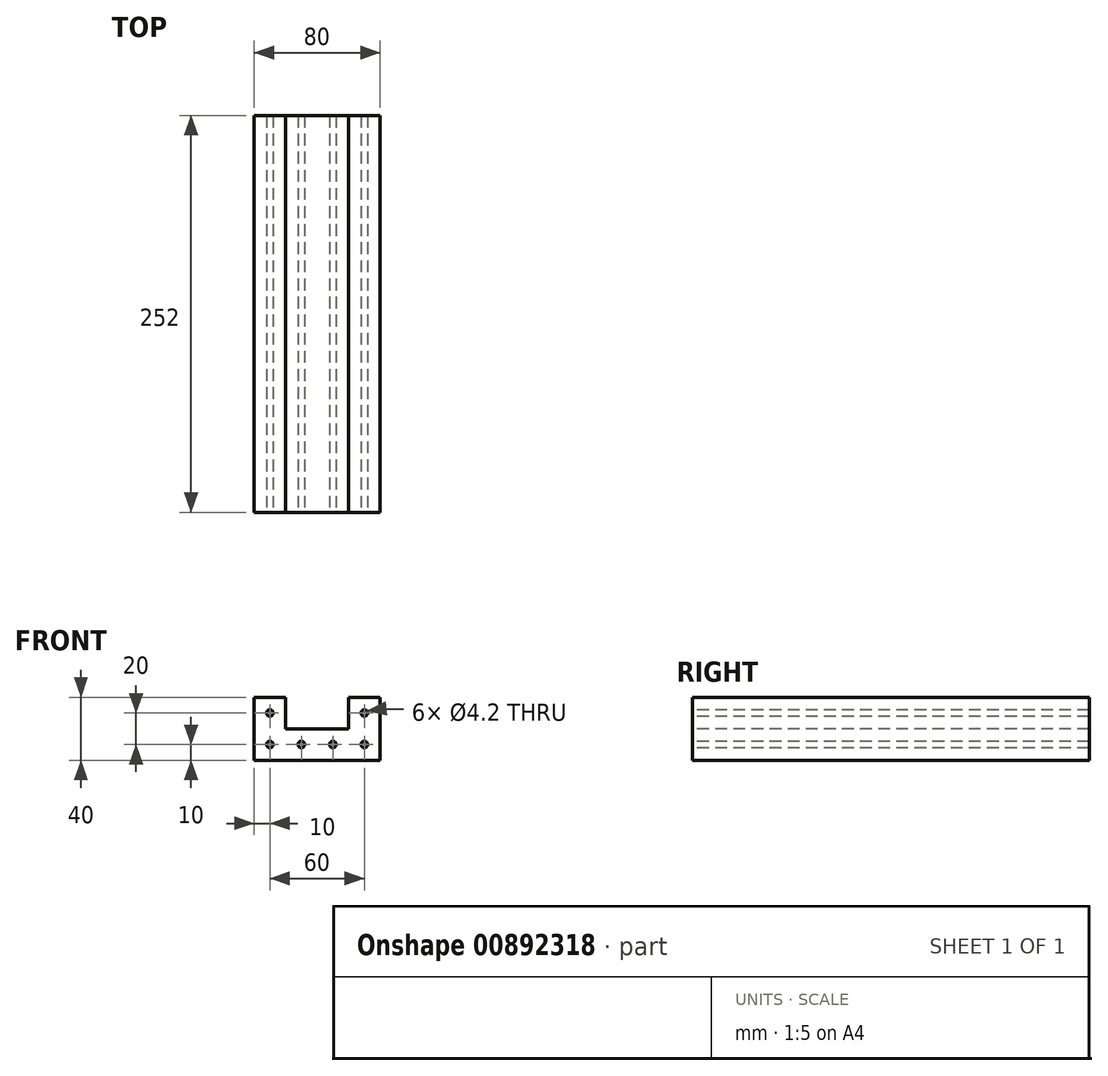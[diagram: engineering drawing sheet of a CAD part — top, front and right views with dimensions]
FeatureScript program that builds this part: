
annotation { "Feature Type Name" : "Feature", "Feature Type Description" : "" }
export const myFeature = defineFeature(function(context is Context, id is Id, definition is map)
    precondition{}
    {
        {
            var Q0;
            Q0=qCreatedBy(makeId("Front.planeOp"),FACE);
            var sketch = newSketch(context, id + "F0", { "sketchPlane" : qUnion([Q0])});
            skLineSegment(sketch, "E0", {"start": v(-40, 40) * mm, "end": v(-40, 0) * mm});
            skLineSegment(sketch, "E1", {"start": v(-40, 0) * mm, "end": v(40, 0) * mm});
            skLineSegment(sketch, "E2", {"start": v(40, 0) * mm, "end": v(40, 40) * mm});
            skLineSegment(sketch, "E3", {"start": v(40, 40) * mm, "end": v(20, 40) * mm});
            skLineSegment(sketch, "E4", {"start": v(20, 40) * mm, "end": v(20, 20) * mm});
            skLineSegment(sketch, "E5", {"start": v(20, 20) * mm, "end": v(-20, 20) * mm});
            skLineSegment(sketch, "E6", {"start": v(-20, 20) * mm, "end": v(-20, 40) * mm});
            skLineSegment(sketch, "E7", {"start": v(-20, 40) * mm, "end": v(-40, 40) * mm});
            skLineSegment(sketch, "E8", {"start": v(-30, 40) * mm, "end": v(-30, 10) * mm, "construction": true});
            skLineSegment(sketch, "E9", {"start": v(-30, 10) * mm, "end": v(30, 10) * mm, "construction": true});
            skLineSegment(sketch, "E10", {"start": v(30, 10) * mm, "end": v(30, 40) * mm, "construction": true});
            skCircle(sketch, "E11", {"center": v(-30, 30) * mm, "radius": 2.1 * mm});
            skCircle(sketch, "E12", {"center": v(-30, 10) * mm, "radius": 2.1 * mm});
            skCircle(sketch, "E13", {"center": v(-10, 10) * mm, "radius": 2.1 * mm});
            skCircle(sketch, "E14", {"center": v(10, 10) * mm, "radius": 2.1 * mm});
            skCircle(sketch, "E15", {"center": v(30, 10) * mm, "radius": 2.1 * mm});
            skCircle(sketch, "E16", {"center": v(30, 30) * mm, "radius": 2.1 * mm});
            skLineSegment(sketch, "E17", {"start": v(-10, 50.7) * mm, "end": v(-10, -33.6) * mm, "construction": true});
            skLineSegment(sketch, "E18", {"start": v(10, 49.6) * mm, "end": v(10, -34.7) * mm, "construction": true});
            skLineSegment(sketch, "E19", {"start": v(-13.39, 22.89) * mm, "end": v(-13.39, -3.46) * mm, "construction": true});
            skLineSegment(sketch, "E20", {"start": v(-6.61, 23.37) * mm, "end": v(-6.61, -3.7) * mm, "construction": true});
            skLineSegment(sketch, "E21", {"start": v(-42.95, 1.8) * mm, "end": v(46.71, 1.8) * mm, "construction": true});
            skSolve(sketch);
        }
        {
            var Q0;
            Q0 = qSketchRegion(id + "F0", true);
            extrude(context, id + "F1", {"entities" : qUnion([Q0]), "oppositeDirection" : true, "depth" : 252 * mm, "offsetDistance" : 25 * mm});
        }
    });
